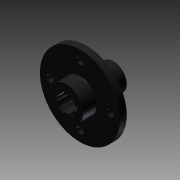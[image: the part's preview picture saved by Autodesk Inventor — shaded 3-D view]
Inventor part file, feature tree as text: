
AUTODESK INVENTOR PART (.ipt)
format: ipt  version: 2011 (Build 150239000, 239)  size: 174,080 bytes
history: native  units: mm (DEFAULTED — no unit token found)
features: sketch x8, extrude x5, hole x3, pattern_circular x2, fillet x1
ambient origin geometry x8: Origin, YZ Plane, XZ Plane, XY Plane, X Axis, Y Axis, Z Axis, Center Point
bodies: Solid1 (feature_tree)
feature tree (19):
  extrude  "Extrusion1"  Depth=76.2mm
  hole  "Mounting Hole"  [1 undecoded]
  pattern_circular  "Circular Pattern1"  Count=4 Angle=360.0deg
  extrude  "Extrusion2"  Depth=12.7mm TaperAngle=0.0deg
  hole  "Hole3"  [1 undecoded]
  extrude  "Extrusion3"  Depth=25.4mm
  pattern_circular  "Circular Pattern2"  [2 undecoded]
  extrude  "Extrusion4"  Depth=28.575mm TaperAngle=0.0deg
  extrude  "Extrusion5"  Depth=0.508mm
  hole  "Hole2"  [1 undecoded]
  fillet  "Fillet1"  Radius=4.0mm
  sketch  "Sketch1"  dims[d0=6.35mm d1=0.0mm d2=76.2mm]
  sketch  "Sketch2"  dims[d3=0.0mm d4=28.575mm]
  sketch  "Sketch3"  dims[d5=6.35mm d6=12.7mm d7=9.525mm d8=6.35mm d9=14.3117mm d10=19.05mm d11=20.594885mm d12=40.0mm d14=360.0deg]
  sketch  "Sketch4"  dims[d15=31.75mm d17=12.7mm d18=0.0mm]
  sketch  "Sketch5"  dims[d22=12.7mm d23=0.0mm d24=60.0mm d26=360.0deg]
  sketch  "Sketch6"  dims[d27=29.845mm d28=25.4mm d29=-0.872665mm]
  sketch  "Sketch7"  dims[d31=16.0mm]
  sketch  "Sketch8"  dims[d32=4.7625mm d33=10.31875mm d34=28.575mm d35=0.0mm d36=9.525mm d37=12.7mm d38=9.525mm d39=6.35mm d40=14.3117mm d41=19.05mm d42=20.594885mm d43=0.508mm d46=60.0deg d47=4.0mm d48=20.0mm d49=16.2mm d50=12.7mm d51=9.525mm d52=6.35mm d53=14.3117mm d54=14.986mm d55=0.0mm]
note: 5 required parameter values undecoded (feature->parameter linkage not recoverable at this tier; creation-order binding heuristic only, values carry confidence <= 0.55)
